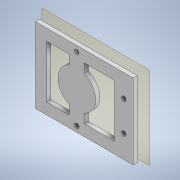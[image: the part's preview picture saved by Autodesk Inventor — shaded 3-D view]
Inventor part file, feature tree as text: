
AUTODESK INVENTOR PART (.ipt)
format: ipt  version: 2022 (Build 260153000, 153)  size: 166,912 bytes
history: native  units: mm
features: extrude x6, sketch x5, other x1, plane x1
ambient origin geometry x8: Origin, YZ Plane, XZ Plane, XY Plane, X Axis, Y Axis, Z Axis, Center Point
bodies: Body1 (feature_tree)
feature tree (13):
  other  "Sólido1"
  extrude  "Extrusión1"  Depth=100.0mm
  sketch  "Boceto2"  dims[d2=100.0mm d3=70.0mm]
  extrude  "Extrusión2"  Depth=70.0mm
  extrude  "Extrusión3"  Depth=20.0mm
  plane  "Plano de trabajo1"
  extrude  "Extrusión7"  Depth=30.0mm TaperAngle=0.0deg
  extrude  "Extrusión13"  [1 undecoded]
  extrude  "Extrusión14"  Depth=5.5mm TaperAngle=0.0deg
  sketch  "Boceto1"  dims[d0=130.0mm d1=100.0mm]
  sketch  "Boceto6"  dims[d4=30.0mm d5=0.0mm d6=20.0mm]
  sketch  "Boceto13"  dims[d7=10.0mm d8=30.0mm d9=0.0mm]
  sketch  "Boceto14"  dims[d10=30.0mm d11=0.0mm d24=-15.0mm d25=9.5mm d26=0.0mm d50=20.0mm d51=0.0mm d52=20.0mm d53=6.0mm d54=6.0mm d55=9.5mm d56=0.0mm d57=50.0mm d58=5.5mm d59=0.0mm d44=0.5mm d45=0.872665mm d46=0.5mm d47=0.872665mm]
note: 1 required parameter value undecoded (feature->parameter linkage not recoverable at this tier; creation-order binding heuristic only, values carry confidence <= 0.55)
